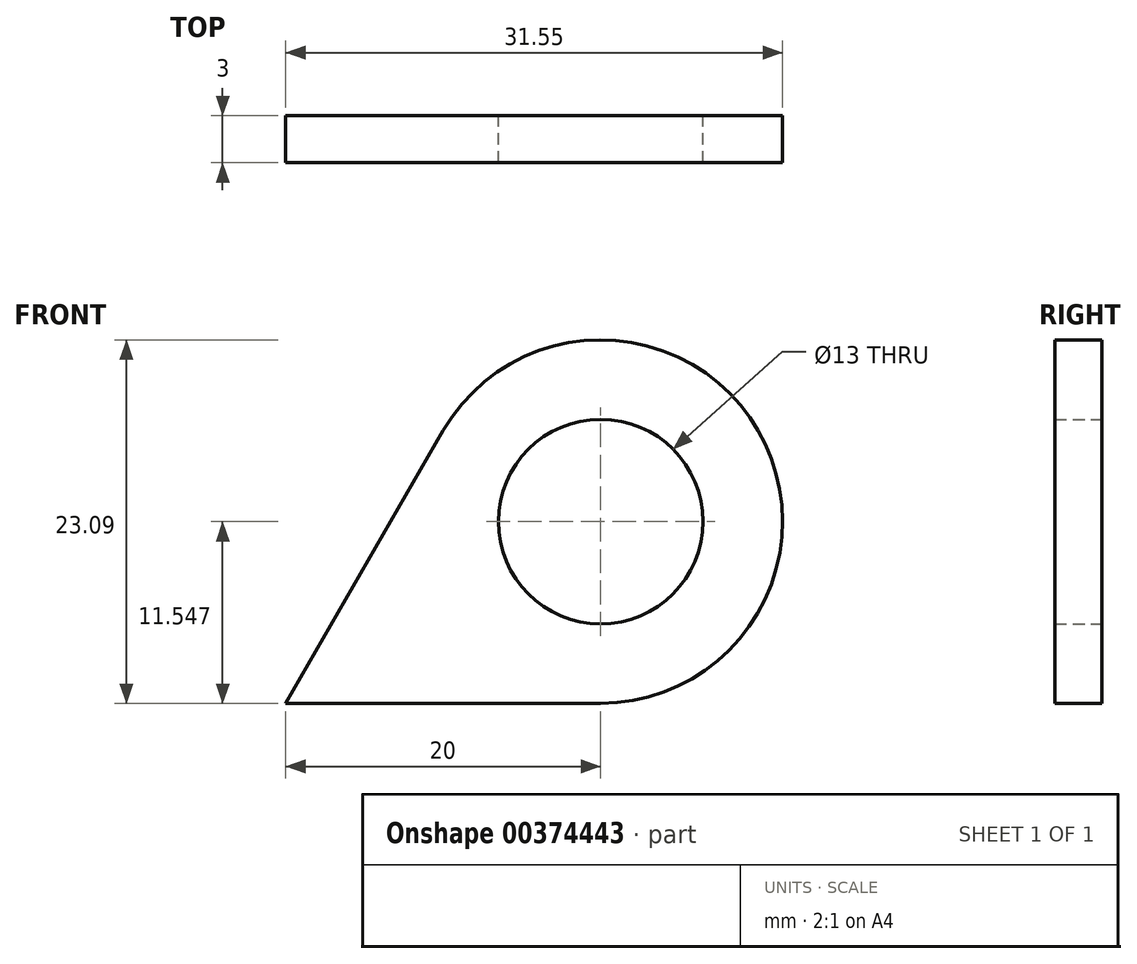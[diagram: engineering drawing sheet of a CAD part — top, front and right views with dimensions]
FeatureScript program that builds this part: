
annotation { "Feature Type Name" : "Feature", "Feature Type Description" : "" }
export const myFeature = defineFeature(function(context is Context, id is Id, definition is map)
    precondition{}
    {
        {
            var Q0;
            Q0=qCreatedBy(makeId("Front.planeOp"),FACE);
            var sketch = newSketch(context, id + "F0", { "sketchPlane" : qUnion([Q0])});
            skLineSegment(sketch, "E0", {"start": v(0, 0) * mm, "end": v(20, 0) * mm});
            skLineSegment(sketch, "E1", {"start": v(0, 0) * mm, "end": v(10, 17.32) * mm});
            skArc(sketch, "E2", {"start": v(20, 0) * mm, "mid": v(30, 17.32) * mm, "end": v(10, 17.32) * mm});
            skCircle(sketch, "E3", {"center": v(20, 11.55) * mm, "radius": 6.5 * mm});
            skSolve(sketch);
        }
        {
            var Q0;
            Q0 = qSketchRegion(id + "F0", true);
            extrude(context, id + "F1", {"entities" : qUnion([Q0]), "depth" : 3 * mm});
        }
    });
